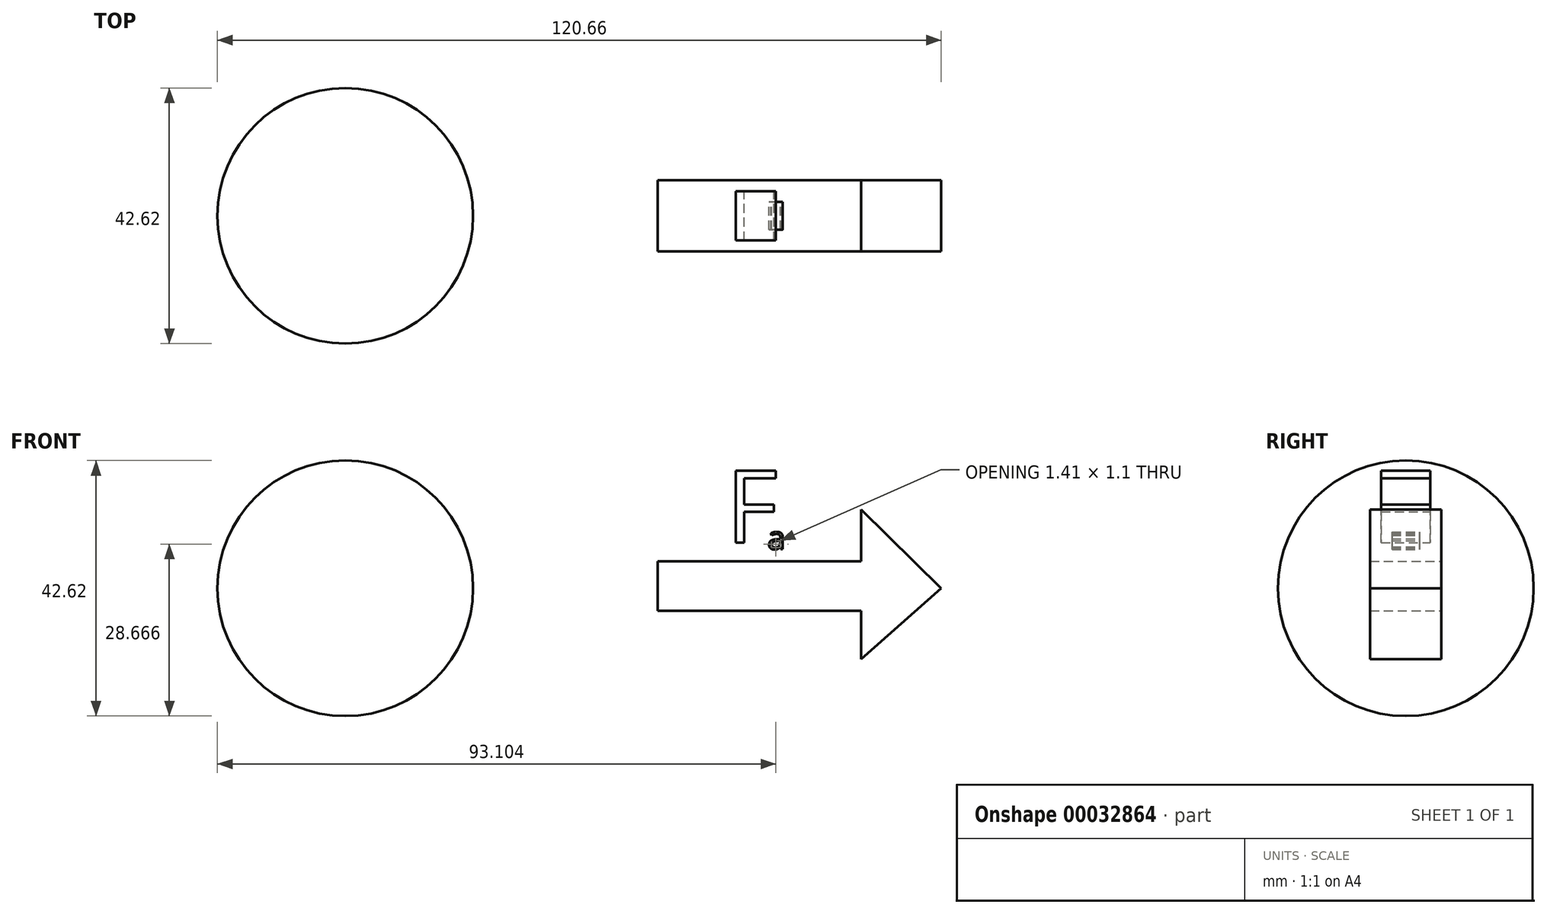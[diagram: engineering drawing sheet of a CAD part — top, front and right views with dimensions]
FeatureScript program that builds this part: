
annotation { "Feature Type Name" : "Feature", "Feature Type Description" : "" }
export const myFeature = defineFeature(function(context is Context, id is Id, definition is map)
    precondition{}
    {
        {
            var Q0;
            Q0=qCreatedBy(makeId("Front.planeOp"),FACE);
            var sketch = newSketch(context, id + "F0", { "sketchPlane" : qUnion([Q0])});
            skArc(sketch, "E0", {"start": v(-19.2, 0) * mm, "mid": v(-40.5, 21.31) * mm, "end": v(-61.82, 0) * mm});
            skLineSegment(sketch, "E1", {"start": v(-68.19, 0) * mm, "end": v(-11.73, 0) * mm});
            skSolve(sketch);
        }
        {
            var Q0;
            {var subQ1=sQuery(id+"F0.wireOp",EDGE,"E0");Q0=makeQuery(id+"F0.imprint","IMPRINT",FACE,{"disambiguationData":[TD([[makeQuery(id+"F0.imprint","IMPRINT",EDGE,{"derivedFrom":subQ1}),1.0]])]});}
            var Q1;
            Q1=sQuery(id+"F0.wireOp",EDGE,"E1");
            revolve(context, id + "F1", {"entities" : qUnion([Q0]), "axis" : qUnion([Q1]), "revolveType" : RevolveType.FULL});
        }
        {
            var Q0;
            Q0=qCreatedBy(makeId("Front.planeOp"),FACE);
            var sketch = newSketch(context, id + "F2", { "sketchPlane" : qUnion([Q0])});
            skLineSegment(sketch, "E2.bottom", {"start": v(11.55, 4.5) * mm, "end": v(45.46, 4.5) * mm});
            skLineSegment(sketch, "E2.top", {"start": v(11.55, -3.76) * mm, "end": v(45.46, -3.76) * mm});
            skLineSegment(sketch, "E2.left", {"start": v(11.55, 4.5) * mm, "end": v(11.55, -3.76) * mm});
            skLineSegment(sketch, "E3", {"start": v(45.46, 13.1) * mm, "end": v(45.46, 4.5) * mm});
            skLineSegment(sketch, "E4", {"start": v(45.46, -11.82) * mm, "end": v(58.84, 0) * mm});
            skLineSegment(sketch, "E5", {"start": v(58.84, 0) * mm, "end": v(45.46, 13.1) * mm});
            skLineSegment(sketch, "E6.trimOffspring", {"start": v(45.46, -3.76) * mm, "end": v(45.46, -11.82) * mm});
            skSolve(sketch);
        }
        {
            var Q0;
            Q0=makeQuery(id+"F2.imprint","IMPRINT",FACE,{"disambiguationData":[TD([[makeQuery(id+"F2.imprint","IMPRINT",EDGE,{"derivedFrom":sQuery(id+"F2.wireOp",EDGE,"E2.bottom")}),-1.0]])]});
            extrude(context, id + "F3", {"entities" : qUnion([Q0]), "endBound" : BoundingType.SYMMETRIC, "depth" : 11.9 * mm});
        }
        {
            var Q0;
            Q0=qCreatedBy(makeId("Front.planeOp"),FACE);
            var sketch = newSketch(context, id + "F4", { "sketchPlane" : qUnion([Q0])});
            skText(sketch, "E7", { "text": "F", "fontName": "OpenSans-Regular.ttf"});
            const initialGuessF4  = {"E7": [0.02291, 0.0076, 1, 0, 0.0121]};
            skSetInitialGuess(sketch, initialGuessF4);
            skSolve(sketch);
        }
        {
            var Q0;
            Q0=qCreatedBy(makeId("Front.planeOp"),FACE);
            var sketch = newSketch(context, id + "F5", { "sketchPlane" : qUnion([Q0])});
            skText(sketch, "E8", { "text": "a", "fontName": "OpenSans-Regular.ttf"});
            const initialGuessF5  = {"E8": [0.02988, 0.0065, 1, 0, 0.00385]};
            skSetInitialGuess(sketch, initialGuessF5);
            skSolve(sketch);
        }
        {
            var Q0;
            Q0 = qSketchRegion(id + "F4", true);
            extrude(context, id + "F6", {"entities" : qUnion([Q0]), "endBound" : BoundingType.SYMMETRIC, "depth" : 8.21 * mm});
        }
        {
            var Q0;
            Q0 = qSketchRegion(id + "F5", true);
            extrude(context, id + "F7", {"entities" : qUnion([Q0]), "endBound" : BoundingType.SYMMETRIC, "depth" : 4.6 * mm});
        }
    });
